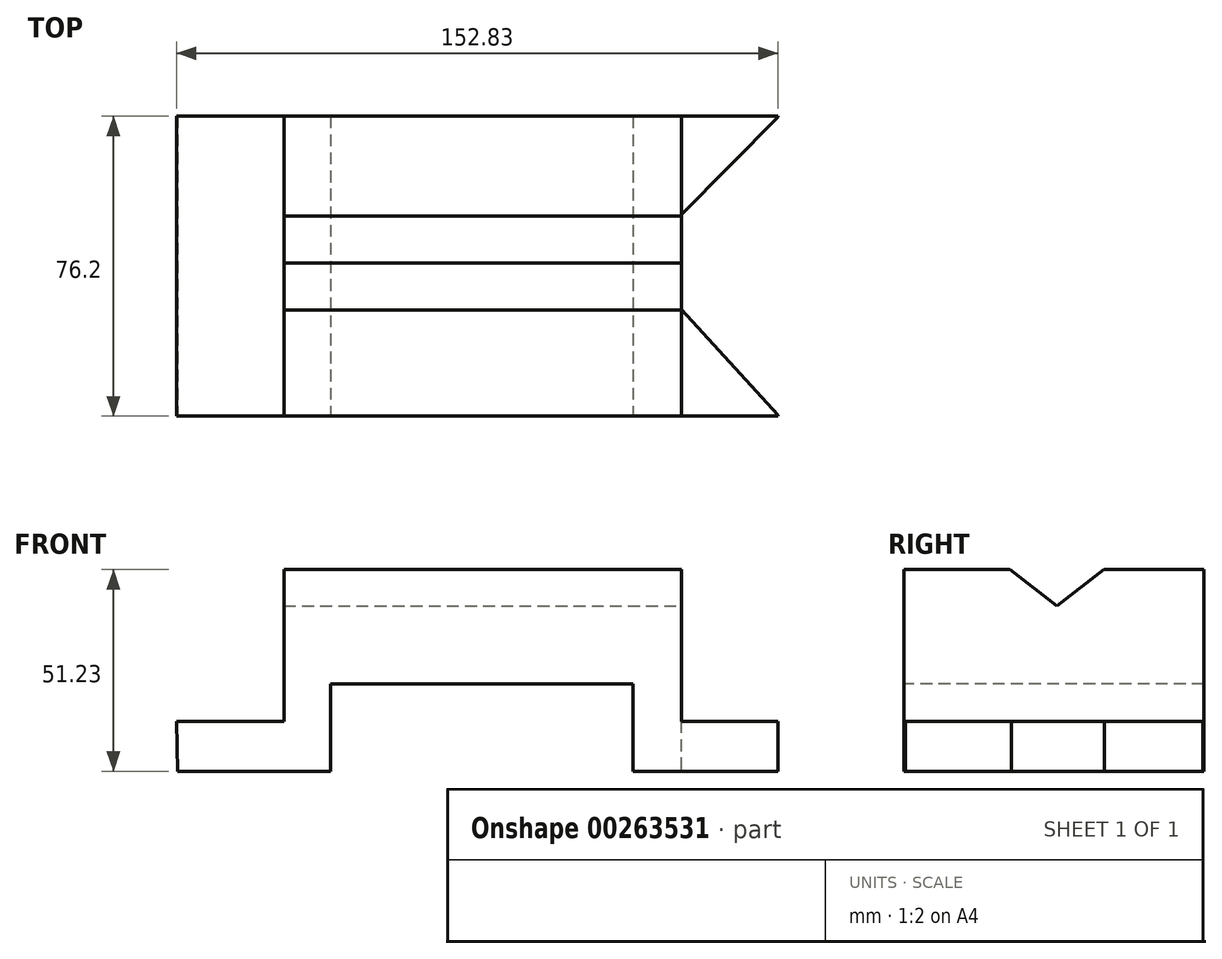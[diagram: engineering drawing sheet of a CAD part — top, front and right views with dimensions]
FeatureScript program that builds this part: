
annotation { "Feature Type Name" : "Feature", "Feature Type Description" : "" }
export const myFeature = defineFeature(function(context is Context, id is Id, definition is map)
    precondition{}
    {
        {
            var Q0;
            Q0=qCreatedBy(makeId("Front.planeOp"),FACE);
            var sketch = newSketch(context, id + "F0", { "sketchPlane" : qUnion([Q0])});
            skLineSegment(sketch, "E0", {"start": v(-72.24, 0) * mm, "end": v(80.3, 0) * mm});
            skLineSegment(sketch, "E1", {"start": v(80.3, 0) * mm, "end": v(80.3, 12.66) * mm});
            skLineSegment(sketch, "E2", {"start": v(80.3, 12.66) * mm, "end": v(55.83, 12.66) * mm});
            skLineSegment(sketch, "E3", {"start": v(55.83, 12.66) * mm, "end": v(55.83, 51.23) * mm});
            skLineSegment(sketch, "E4", {"start": v(55.83, 51.23) * mm, "end": v(-45.19, 51.23) * mm});
            skLineSegment(sketch, "E5", {"start": v(-45.19, 51.23) * mm, "end": v(-45.19, 12.66) * mm});
            skLineSegment(sketch, "E6", {"start": v(-45.19, 12.66) * mm, "end": v(-72.53, 12.66) * mm});
            skLineSegment(sketch, "E7", {"start": v(-72.53, 12.66) * mm, "end": v(-72.24, 0) * mm});
            skLineSegment(sketch, "E8.bottom", {"start": v(-33.35, 22.16) * mm, "end": v(43.5, 22.16) * mm});
            skLineSegment(sketch, "E8.top", {"start": v(-33.35, 0) * mm, "end": v(43.5, 0) * mm});
            skLineSegment(sketch, "E8.left", {"start": v(-33.35, 22.16) * mm, "end": v(-33.35, 0) * mm});
            skLineSegment(sketch, "E8.right", {"start": v(43.5, 22.16) * mm, "end": v(43.5, 0) * mm});
            skSolve(sketch);
        }
        {
            var Q0;
            {var subQ4=sQuery(id+"F0.wireOp",EDGE,"E1");Q0=makeQuery(id+"F0.imprint","IMPRINT",FACE,{"disambiguationData":[TD([[makeQuery(id+"F0.imprint","IMPRINT",EDGE,{"derivedFrom":subQ4}),1.0]])]});}
            extrude(context, id + "F1", {"entities" : qUnion([Q0]), "oppositeDirection" : true, "depth" : 76.2 * mm});
        }
        {
            var Q0;
            Q0=qCreatedBy(makeId("Right.planeOp"),FACE);
            var sketch = newSketch(context, id + "F2", { "sketchPlane" : qUnion([Q0])});
            skLineSegment(sketch, "E9", {"start": v(38.9, 51.8) * mm, "end": v(51.6, 51.8) * mm});
            skLineSegment(sketch, "E10", {"start": v(51.6, 51.8) * mm, "end": v(38.9, 42.02) * mm});
            skLineSegment(sketch, "E11", {"start": v(38.9, 42.02) * mm, "end": v(26.2, 51.8) * mm});
            skLineSegment(sketch, "E12", {"start": v(26.2, 51.8) * mm, "end": v(38.9, 51.8) * mm});
            skSolve(sketch);
        }
        {
            var Q0;
            Q0=makeQuery(id+"F2.imprint","IMPRINT",FACE,{"disambiguationData":[TD([[makeQuery(id+"F2.imprint","IMPRINT",EDGE,{"derivedFrom":sQuery(id+"F2.wireOp",EDGE,"E9")}),-1.0]])]});
            extrude(context, id + "F3", {"entities" : qUnion([Q0]), "operationType" : NewBodyOperationType.REMOVE, "oppositeDirection" : true, "depth" : 50.8 * mm});
        }
        {
            var Q0;
            Q0=makeQuery(id+"F3.boolean.opBoolean","COPY",FACE,{"derivedFrom":makeQuery(id+"F3.opExtrude","CAP_FACE",FACE,{"disambiguationData":[OSD([sQuery(id+"F2.wireOp",EDGE,"E9"),sQuery(id+"F2.wireOp",EDGE,"E10"),sQuery(id+"F2.wireOp",EDGE,"E11"),sQuery(id+"F2.wireOp",EDGE,"E12")])],"isStart":true})});
            extrude(context, id + "F4", {"entities" : qUnion([Q0]), "operationType" : NewBodyOperationType.REMOVE, "oppositeDirection" : true, "depth" : 76.2 * mm});
        }
        {
            var Q0;
            Q0=qCreatedBy(makeId("Top.planeOp"),FACE);
            var sketch = newSketch(context, id + "F5", { "sketchPlane" : qUnion([Q0])});
            skPoint(sketch, "E13.start.orphan", {"position": v(-47.07, 0) * mm});
            skLineSegment(sketch, "E14", {"start": v(80.6, 0) * mm, "end": v(55.6, 27.36) * mm});
            skLineSegment(sketch, "E15", {"start": v(80.6, 76.26) * mm, "end": v(55.6, 51) * mm});
            skLineSegment(sketch, "E16", {"start": v(80.6, 76.26) * mm, "end": v(80.6, 0) * mm});
            skLineSegment(sketch, "E17", {"start": v(55.6, 51) * mm, "end": v(55.6, 27.36) * mm});
            skPoint(sketch, "E18.start.orphan", {"position": v(55.6, 0) * mm});
            skSolve(sketch);
        }
        {
            var Q0;
            Q0 = qSketchRegion(id + "F5", true);
            extrude(context, id + "F6", {"entities" : qUnion([Q0]), "operationType" : NewBodyOperationType.REMOVE, "depth" : 12.7 * mm});
        }
    });
